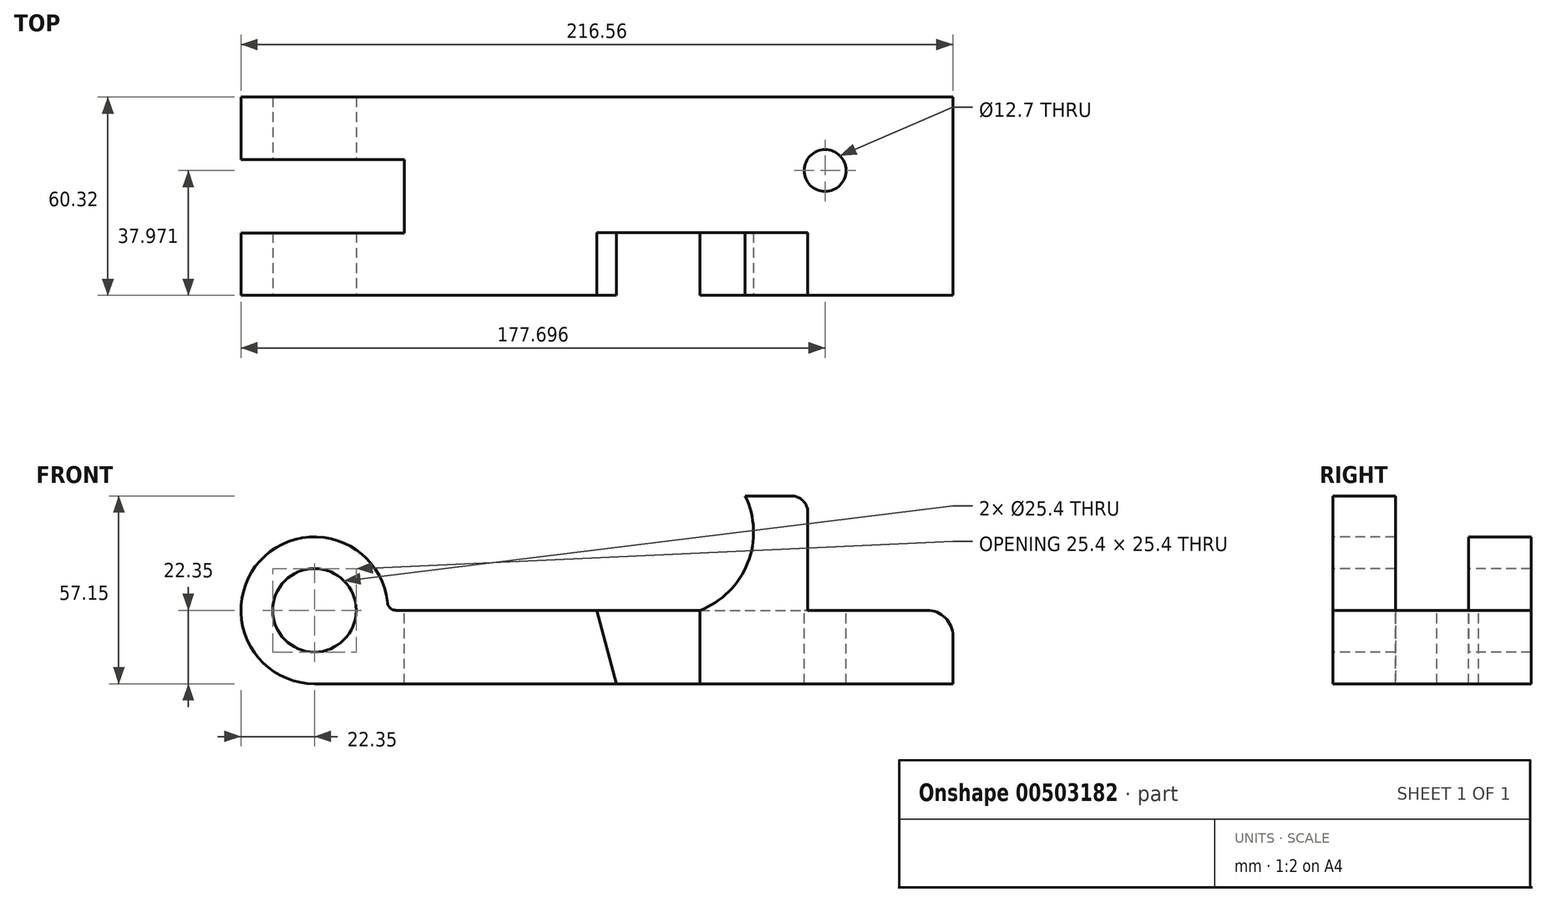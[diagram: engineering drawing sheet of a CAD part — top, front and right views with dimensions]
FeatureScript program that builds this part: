
annotation { "Feature Type Name" : "Feature", "Feature Type Description" : "" }
export const myFeature = defineFeature(function(context is Context, id is Id, definition is map)
    precondition{}
    {
        {
            var Q0;
            Q0=qCreatedBy(makeId("Front.planeOp"),FACE);
            var sketch = newSketch(context, id + "F0", { "sketchPlane" : qUnion([Q0])});
            skCircle(sketch, "E0", {"center": v(0, 0) * mm, "radius": 12.7 * mm});
            skLineSegment(sketch, "E1.bottom", {"start": v(0, 0) * mm, "end": v(194.2, 0) * mm});
            skLineSegment(sketch, "E1.top", {"start": v(0, -22.35) * mm, "end": v(194.2, -22.35) * mm});
            skLineSegment(sketch, "E1.left", {"start": v(0, 0) * mm, "end": v(0, -22.35) * mm});
            skLineSegment(sketch, "E1.right", {"start": v(194.2, 0) * mm, "end": v(194.2, -22.35) * mm});
            skArc(sketch, "E2", {"start": v(22.35, 0) * mm, "mid": v(-15.8, 15.8) * mm, "end": v(0, -22.35) * mm});
            skLineSegment(sketch, "E3", {"start": v(117.25, 0) * mm, "end": v(117.25, -22.35) * mm});
            skLineSegment(sketch, "E4", {"start": v(85.85, 0) * mm, "end": v(91.85, -22.35) * mm});
            skLineSegment(sketch, "E5", {"start": v(150.09, 0) * mm, "end": v(150.09, 34.8) * mm});
            skLineSegment(sketch, "E6", {"start": v(131.04, 34.8) * mm, "end": v(150.09, 34.8) * mm});
            skArc(sketch, "E7", {"start": v(117.25, 0) * mm, "mid": v(131.8, 14.37) * mm, "end": v(131.04, 34.8) * mm});
            skSolve(sketch);
        }
        {
            var Q0;
            {var subQ5=sQuery(id+"F0.wireOp",EDGE,"E2");Q0=makeQuery(id+"F0.imprint","IMPRINT",FACE,{"disambiguationData":[TD([[makeQuery(id+"F0.imprint","IMPRINT",EDGE,{"derivedFrom":subQ5}),1.0]])]});}
            var Q1;
            {var subQ3=sQuery(id+"F0.wireOp",EDGE,"E4");Q1=makeQuery(id+"F0.imprint","IMPRINT",FACE,{"disambiguationData":[TD([[makeQuery(id+"F0.imprint","IMPRINT",EDGE,{"derivedFrom":subQ3}),-1.0]])]});}
            var Q2;
            {var subQ0=sQuery(id+"F0.wireOp",EDGE,"E3");Q2=makeQuery(id+"F0.imprint","IMPRINT",FACE,{"disambiguationData":[TD([[makeQuery(id+"F0.imprint","IMPRINT",EDGE,{"derivedFrom":subQ0}),-1.0]])]});}
            var Q3;
            {var subQ0=sQuery(id+"F0.wireOp",EDGE,"E1.right");Q3=makeQuery(id+"F0.imprint","IMPRINT",FACE,{"disambiguationData":[TD([[makeQuery(id+"F0.imprint","IMPRINT",EDGE,{"derivedFrom":subQ0}),-1.0]])]});}
            extrude(context, id + "F1", {"entities" : qUnion([Q0, Q1, Q2, Q3]), "endBound" : BoundingType.SYMMETRIC, "oppositeDirection" : true, "depth" : 60.32 * mm});
        }
        {
            var Q0;
            Q0=makeQuery(id+"F1.opExtrude","CAP_FACE",FACE,{"disambiguationData":[OSD([sQuery(id+"F0.wireOp",EDGE,"E0"),sQuery(id+"F0.wireOp",EDGE,"E1.bottom"),sQuery(id+"F0.wireOp",EDGE,"E1.top"),sQuery(id+"F0.wireOp",EDGE,"E1.right"),sQuery(id+"F0.wireOp",EDGE,"E2")])],"isStart":true});
            var sketch = newSketch(context, id + "F2", { "sketchPlane" : qUnion([Q0])});
            skLineSegment(sketch, "E8.0", {"start": v(131.04, 34.8) * mm, "end": v(150.09, 34.8) * mm});
            skLineSegment(sketch, "E9.0", {"start": v(150.09, 0) * mm, "end": v(150.09, 34.8) * mm});
            skArc(sketch, "E10.0", {"start": v(117.25, 0) * mm, "mid": v(131.8, 14.37) * mm, "end": v(131.04, 34.8) * mm});
            skLineSegment(sketch, "E11.0", {"start": v(117.25, 0) * mm, "end": v(117.25, -22.35) * mm});
            skLineSegment(sketch, "E12.0", {"start": v(85.85, 0) * mm, "end": v(91.85, -22.35) * mm});
            skLineSegment(sketch, "E13", {"start": v(85.85, 0) * mm, "end": v(117.25, 0) * mm});
            skLineSegment(sketch, "E14", {"start": v(91.85, -22.35) * mm, "end": v(117.25, -22.35) * mm});
            skLineSegment(sketch, "E15", {"start": v(117.25, 0) * mm, "end": v(150.09, 0) * mm});
            skSolve(sketch);
        }
        {
            var Q0;
            Q0=makeQuery(id+"F2.imprint","IMPRINT",FACE,{"disambiguationData":[TD([[makeQuery(id+"F2.imprint","IMPRINT",EDGE,{"derivedFrom":sQuery(id+"F2.wireOp",EDGE,"E11.0")}),-1.0]])]});
            extrude(context, id + "F3", {"entities" : qUnion([Q0]), "operationType" : NewBodyOperationType.REMOVE, "oppositeDirection" : true, "depth" : 19.05 * mm});
        }
        {
            var Q0;
            Q0=makeQuery(id+"F2.imprint","IMPRINT",FACE,{"disambiguationData":[TD([[makeQuery(id+"F2.imprint","IMPRINT",EDGE,{"derivedFrom":sQuery(id+"F2.wireOp",EDGE,"E8.0")}),-1.0]])]});
            extrude(context, id + "F4", {"entities" : qUnion([Q0]), "operationType" : NewBodyOperationType.ADD, "oppositeDirection" : true, "depth" : 19.05 * mm});
        }
        {
            var Q0;
            Q0=makeQuery(id+"F4.opExtrude","SWEPT_EDGE",EDGE,{"disambiguationData":[OSD([sQuery(id+"F2.wireOp",EDGE,"E8.0"),sQuery(id+"F2.wireOp",EDGE,"E9.0")])]});
            fillet(context, id + "F5", {"entities" : qUnion([Q0]), "radius" : 5.08 * mm, "tangentPropagation" : true, "allowEdgeOverflow" : false});
        }
        {
            var Q0;
            Q0=makeQuery(id+"F4.opExtrude","SWEPT_EDGE",EDGE,{"disambiguationData":[OSD([sQuery(id+"F0.wireOp",EDGE,"E1.bottom"),sQuery(id+"F2.wireOp",EDGE,"E9.0"),sQuery(id+"F2.wireOp",EDGE,"E15")])]});
            var Q1;
            Q1=makeQuery(id+"F1.opExtrude","SWEPT_EDGE",EDGE,{"disambiguationData":[OSD([sQuery(id+"F0.wireOp",EDGE,"E1.bottom"),sQuery(id+"F0.wireOp",EDGE,"E2")])]});
            fillet(context, id + "F6", {"entities" : qUnion([Q0, Q1]), "radius" : 2.54 * mm, "tangentPropagation" : true, "allowEdgeOverflow" : false});
        }
        {
            var Q0;
            Q0=qCreatedBy(makeId("Top.planeOp"),FACE);
            var sketch = newSketch(context, id + "F7", { "sketchPlane" : qUnion([Q0])});
            skCircle(sketch, "E16", {"center": v(155.35, 7.81) * mm, "radius": 6.35 * mm});
            skLineSegment(sketch, "E17.bottom", {"start": v(27.41, 11.16) * mm, "end": v(-26.84, 11.16) * mm});
            skLineSegment(sketch, "E17.top", {"start": v(27.41, -11.16) * mm, "end": v(-26.84, -11.16) * mm});
            skLineSegment(sketch, "E17.left", {"start": v(27.41, 11.16) * mm, "end": v(27.41, -11.16) * mm});
            skLineSegment(sketch, "E17.right", {"start": v(-26.84, 11.16) * mm, "end": v(-26.84, -11.16) * mm});
            skPoint(sketch, "E17.middle", {"position": v(0, 0) * mm});
            skSolve(sketch);
        }
        {
            var Q0;
            Q0=makeQuery(id+"F1.opExtrude","SWEPT_EDGE",EDGE,{"disambiguationData":[OSD([sQuery(id+"F0.wireOp",EDGE,"E1.bottom"),sQuery(id+"F0.wireOp",EDGE,"E1.right")])]});
            fillet(context, id + "F8", {"entities" : qUnion([Q0]), "radius" : 7.87 * mm, "tangentPropagation" : true, "allowEdgeOverflow" : false});
        }
        {
            var Q0;
            Q0=makeQuery(id+"F7.imprint","IMPRINT",FACE,{"disambiguationData":[TD([[makeQuery(id+"F7.imprint","IMPRINT",EDGE,{"derivedFrom":sQuery(id+"F7.wireOp",EDGE,"E17.bottom")}),1.0]])]});
            var Q1;
            Q1=makeQuery(id+"F7.imprint","IMPRINT",FACE,{"disambiguationData":[TD([[makeQuery(id+"F7.imprint","IMPRINT",EDGE,{"derivedFrom":sQuery(id+"F7.wireOp",EDGE,"E16")}),1.0]])]});
            extrude(context, id + "F9", {"entities" : qUnion([Q0, Q1]), "operationType" : NewBodyOperationType.REMOVE, "endBound" : BoundingType.SYMMETRIC, "oppositeDirection" : true, "depth" : 95.5 * mm});
        }
    });
